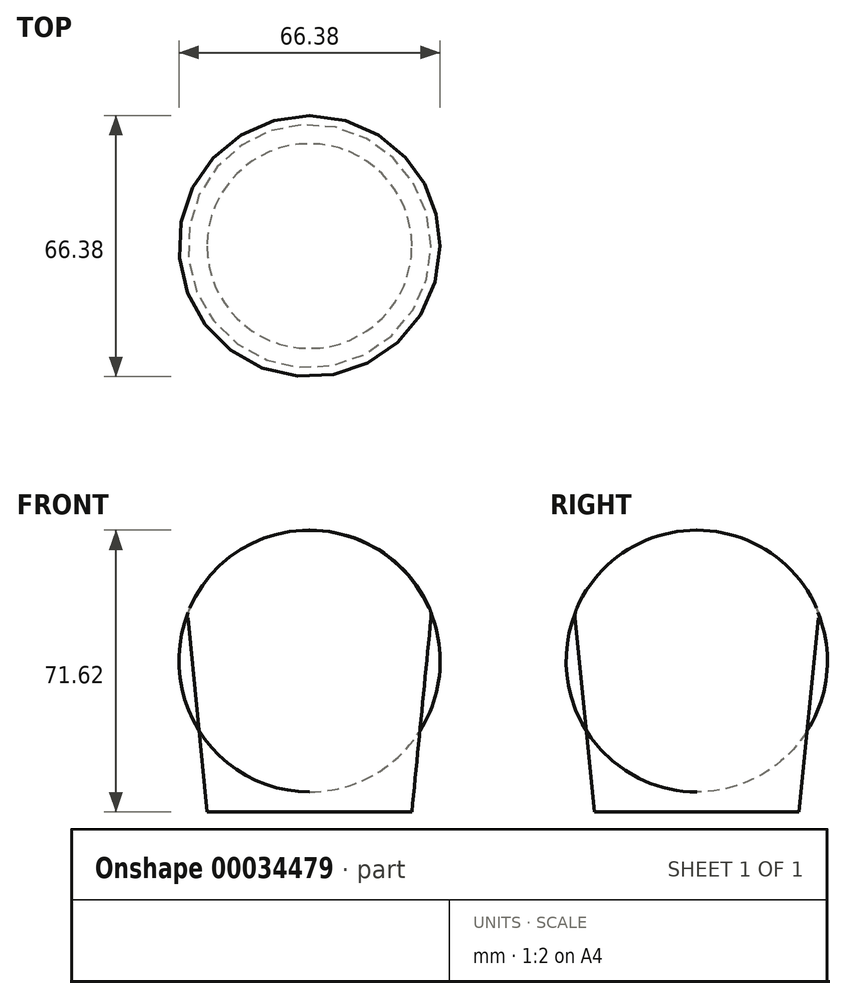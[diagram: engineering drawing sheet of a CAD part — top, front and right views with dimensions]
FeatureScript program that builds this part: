
annotation { "Feature Type Name" : "Feature", "Feature Type Description" : "" }
export const myFeature = defineFeature(function(context is Context, id is Id, definition is map)
    precondition{}
    {
        {
            var Q0;
            Q0=qCreatedBy(makeId("Front.planeOp"),FACE);
            var sketch = newSketch(context, id + "F0", { "sketchPlane" : qUnion([Q0])});
            skLineSegment(sketch, "E0", {"start": v(0, 0) * mm, "end": v(-26, 0) * mm});
            skLineSegment(sketch, "E1", {"start": v(0, 0) * mm, "end": v(0, 71.62) * mm});
            skLineSegment(sketch, "E2", {"start": v(0, 50.57) * mm, "end": v(-31, 50.57) * mm});
            skLineSegment(sketch, "E3", {"start": v(-26, 0) * mm, "end": v(-31, 50.57) * mm});
            skArc(sketch, "E4", {"start": v(0, 71.62) * mm, "mid": v(-18.75, 65.88) * mm, "end": v(-31, 50.57) * mm});
            skSolve(sketch);
        }
        {
            var Q0;
            {var subQ2=sQuery(id+"F0.wireOp",EDGE,"E2");Q0=makeQuery(id+"F0.imprint","IMPRINT",FACE,{"disambiguationData":[TD([[makeQuery(id+"F0.imprint","IMPRINT",EDGE,{"derivedFrom":subQ2}),-1.0]])]});}
            var Q1;
            {var subQ0=sQuery(id+"F0.wireOp",EDGE,"E0");Q1=makeQuery(id+"F0.imprint","IMPRINT",FACE,{"disambiguationData":[TD([[makeQuery(id+"F0.imprint","IMPRINT",EDGE,{"derivedFrom":subQ0}),-1.0]])]});}
            var Q2;
            Q2=sQuery(id+"F0.wireOp",EDGE,"E1");
            revolve(context, id + "F1", {"entities" : qUnion([Q0, Q1]), "axis" : qUnion([Q2]), "revolveType" : RevolveType.FULL});
        }
        {
            var Q0;
            Q0=makeQuery(id+"F1.opRevolve","SWEPT_EDGE",EDGE,{"disambiguationData":[OSD([sQuery(id+"F0.wireOp",EDGE,"E2"),sQuery(id+"F0.wireOp",EDGE,"E3"),sQuery(id+"F0.wireOp",EDGE,"E4")])]});
            fillet(context, id + "F2", {"entities" : qUnion([Q0]), "radius" : 5 * mm, "tangentPropagation" : true, "allowEdgeOverflow" : false});
        }
    });
